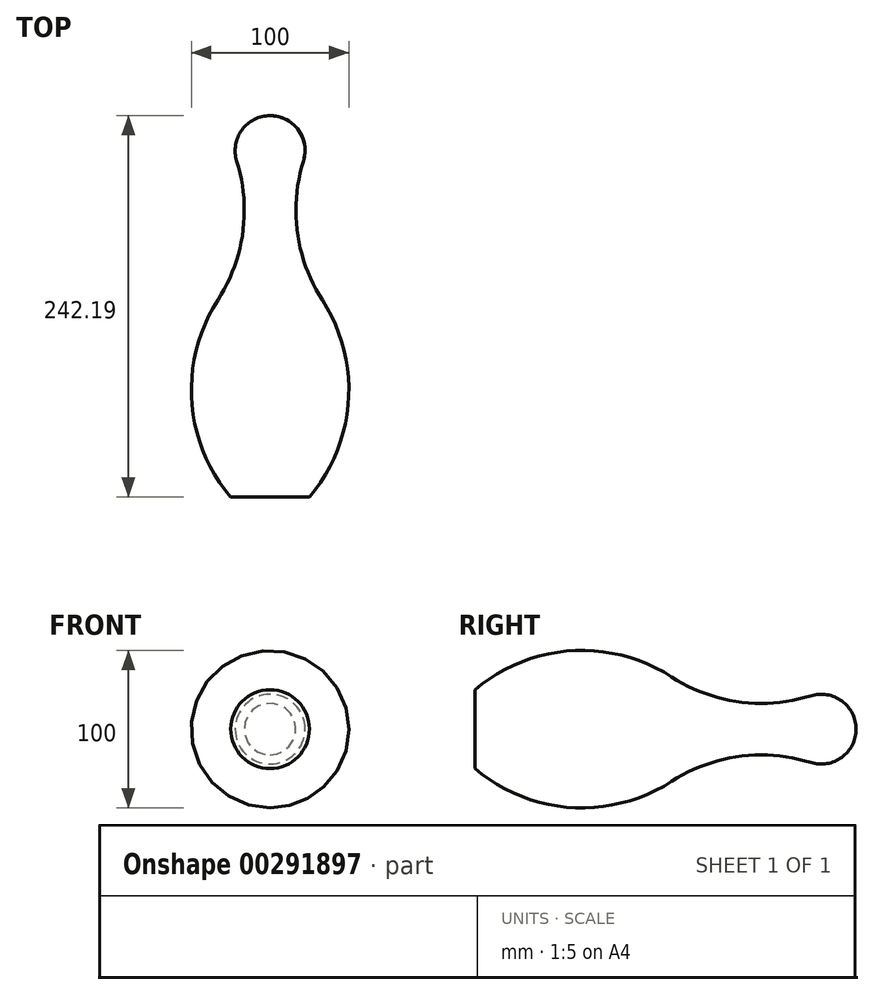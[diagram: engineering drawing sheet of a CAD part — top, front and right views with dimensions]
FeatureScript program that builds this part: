
annotation { "Feature Type Name" : "Feature", "Feature Type Description" : "" }
export const myFeature = defineFeature(function(context is Context, id is Id, definition is map)
    precondition{}
    {
        {
            var Q0;
            Q0=qCreatedBy(makeId("Top.planeOp"),FACE);
            var sketch = newSketch(context, id + "F0", { "sketchPlane" : qUnion([Q0])});
            skArc(sketch, "E0", {"start": v(0, 242.2) * mm, "mid": v(-17.88, 233.14) * mm, "end": v(-21.18, 213.37) * mm});
            skLineSegment(sketch, "E1", {"start": v(0, 0) * mm, "end": v(-25, 0) * mm});
            skArc(sketch, "E2", {"start": v(-33.19, 125) * mm, "mid": v(-16.92, 171.33) * mm, "end": v(-23.5, 220) * mm});
            skArc(sketch, "E3", {"start": v(-33.19, 125) * mm, "mid": v(-49.78, 61.14) * mm, "end": v(-25, 0) * mm});
            skLineSegment(sketch, "E4", {"start": v(0, 0) * mm, "end": v(0, 242.2) * mm});
            skSolve(sketch);
        }
        {
            var Q0;
            {var subQ2=sQuery(id+"F0.wireOp",EDGE,"E0");Q0=makeQuery(id+"F0.imprint","IMPRINT",FACE,{"disambiguationData":[TD([[makeQuery(id+"F0.imprint","IMPRINT",EDGE,{"derivedFrom":subQ2}),1.0]])]});}
            var Q1;
            Q1=sQuery(id+"F0.wireOp",EDGE,"E4");
            revolve(context, id + "F1", {"entities" : qUnion([Q0]), "axis" : qUnion([Q1]), "revolveType" : RevolveType.FULL});
        }
    });
